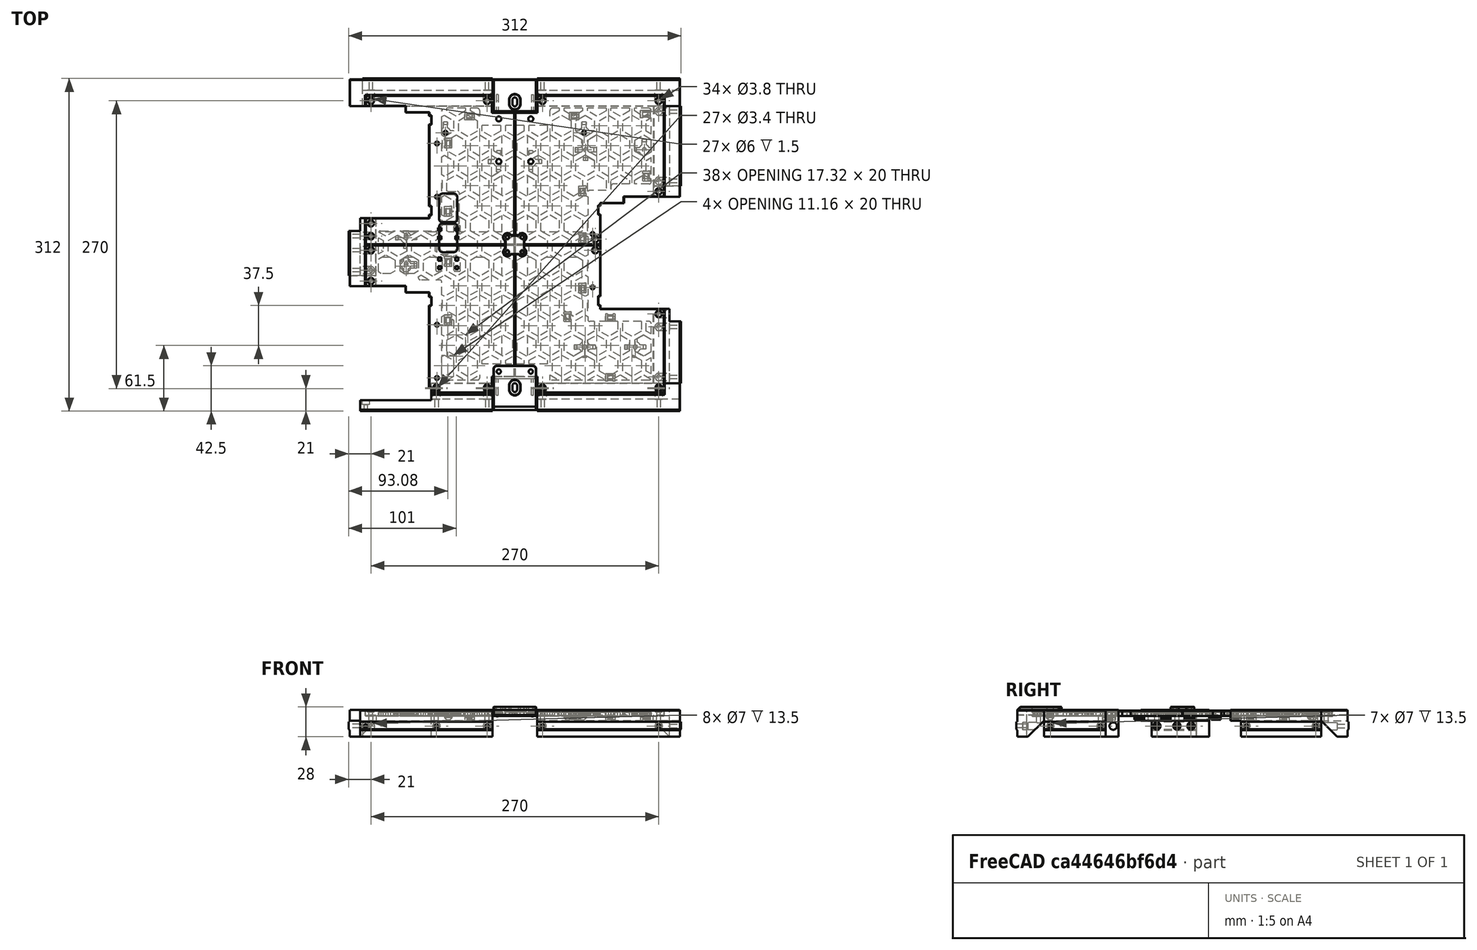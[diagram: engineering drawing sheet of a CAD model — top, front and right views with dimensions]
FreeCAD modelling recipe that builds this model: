
FCSTD DOCUMENT  (FreeCAD 0.19R24291 (Git))
Label: bottom-panel-4pcs
License: Other
LicenseURL: GPL3
objects: Part::Feature×85, Part::MultiFuse×51, Part::Cut×34, Part::Box×30, Part::Cylinder×17, Part::Chamfer×15, Part::Refine×5, Part::Fillet×4, Part::MultiCommon×4, Part::Extrusion×1
note: 246 computed .brp shape members not serialized (recipe doc carries the construction recipe); baked Part::Feature solids carry a one-line shape summary decoded from their .brp

FEATURE [Part::Feature] Chamfer005007002031002  label="origin-uni-body"
  shape: bbox 280 x 279 x 8.5 mm, 1486 faces (baked)
FEATURE [Part::Feature] Cut002015026004001  label="plain-plate"
  shape: bbox 280 x 279 x 5 mm, 52 faces (baked)
FEATURE [Part::Feature] Fusion001010002032002  label="Fusion001010002034"
  Placement = pos=(-26,135,0) rot=(0,0,1;0rad)
  shape: bbox 6 x 6 x 35 mm, 7 faces (baked)
FEATURE [Part::Feature] Fusion001010002032003  label="Fusion001010002035"
  Placement = pos=(26,135,0) rot=(0,0,1;0rad)
  shape: bbox 6 x 6 x 35 mm, 7 faces (baked)
FEATURE [Part::Feature] Fusion001010002032004  label="Fusion001010002036"
  Placement = pos=(135,135,0) rot=(0,0,1;0rad)
  shape: bbox 6 x 6 x 35 mm, 7 faces (baked)
FEATURE [Part::Feature] Fusion001010002032005  label="Fusion001010002037"
  Placement = pos=(135,50,0) rot=(0,0,1;0rad)
  shape: bbox 6 x 6 x 35 mm, 7 faces (baked)
FEATURE [Part::Feature] Fusion001010002032006  label="Fusion001010002038"
  Placement = pos=(135,-65,0) rot=(0,0,1;0rad)
  shape: bbox 6 x 6 x 35 mm, 7 faces (baked)
FEATURE [Part::Feature] Fusion001010002032007  label="Fusion001010002039"
  Placement = pos=(135,-135,0) rot=(0,0,1;0rad)
  shape: bbox 6 x 6 x 35 mm, 7 faces (baked)
FEATURE [Part::Feature] Fusion001010002032008  label="Fusion001010002040"
  Placement = pos=(-26,-135,0) rot=(0,0,1;0rad)
  shape: bbox 6 x 6 x 35 mm, 7 faces (baked)
FEATURE [Part::Feature] Fusion001010002032009  label="Fusion001010002041"
  Placement = pos=(-73.5,-135,0) rot=(0,0,1;0rad)
  shape: bbox 6 x 6 x 35 mm, 7 faces (baked)
FEATURE [Part::Feature] Fusion001010002032010  label="Fusion001010002042"
  Placement = pos=(-135,-34,0) rot=(0,0,1;0rad)
  shape: bbox 6 x 6 x 35 mm, 7 faces (baked)
FEATURE [Part::Feature] Fusion001010002032011  label="Fusion001010002043"
  Placement = pos=(-135,8,0) rot=(0,0,1;0rad)
  shape: bbox 6 x 6 x 35 mm, 7 faces (baked)
FEATURE [Part::Feature] Fusion001010002032012  label="Fusion001010002044"
  Placement = pos=(-135,135,0) rot=(0,0,1;0rad)
  shape: bbox 6 x 6 x 35 mm, 7 faces (baked)
FEATURE [Part::Feature] Fusion001010002032014
  Placement = pos=(26,-135,0) rot=(0,0,1;0rad)
  shape: bbox 6 x 6 x 35 mm, 7 faces (baked)
FEATURE [Part::Box] Box040  label="Cube039"
  AttacherType = Attacher::AttachEngine3D
  Height = 9
  Length = 15
  Placement = pos=(-70,-45,24.5) rot=(0,0,1;0rad)
  Width = 25
FEATURE [Part::Fillet] Fillet001025
  Base = -> Box040
  Edges = 4 edges r=2: [Edge1,Edge3,Edge5,Edge7]
  Placement = pos=(0,39,0) rot=(0,0,1;0rad)
FEATURE [Part::Box] Box046  label="Cube045"
  AttacherType = Attacher::AttachEngine3D
  Height = 10
  Length = 2
  Placement = pos=(-55,-6,24.5) rot=(0,0,1;0rad)
  Width = 3
FEATURE [Part::Box] Box047  label="Cube046"
  AttacherType = Attacher::AttachEngine3D
  Height = 10
  Length = 2
  Placement = pos=(-72,-14,24.5) rot=(0,0,1;0rad)
  Width = 3
FEATURE [Part::Box] Box048  label="Cube047"
  AttacherType = Attacher::AttachEngine3D
  Height = 10
  Length = 2
  Placement = pos=(-72,-6,24.5) rot=(0,0,1;0rad)
  Width = 3
FEATURE [Part::Box] Box049  label="Cube048"
  AttacherType = Attacher::AttachEngine3D
  Height = 10
  Length = 2
  Placement = pos=(-55,-14,24.5) rot=(0,0,1;0rad)
  Width = 3
FEATURE [Part::MultiFuse] Fusion006002011004053036004001028003005014008
  Placement = pos=(0,-9,0) rot=(0,0,1;0rad)
  Shapes = -> [Box046,Box048,Box047,Box049]
FEATURE [Part::MultiFuse] Fusion006002011004053036004001028003005014018004  label="cabling"
  Placement = pos=(0,28,0) rot=(0,0,1;0rad)
  Shapes = -> [Fillet001025,Fusion006002011004053036004001028003005014008]
FEATURE [Part::Feature] Cut002015002
  Placement = pos=(-102,8.5,27.5) rot=(0,1,0;3.14159rad)
  shape: bbox 20 x 20 x 3 mm, 23 faces (baked)
FEATURE [Part::Feature] Cut002015003
  Placement = pos=(-102,-18,27.5) rot=(0,1,0;3.14159rad)
  shape: bbox 20 x 20 x 3 mm, 23 faces (baked)
FEATURE [Part::Feature] Cut002015004
  Placement = pos=(113,-96,27.5) rot=(0,1,0;3.14159rad)
  shape: bbox 20 x 20 x 3 mm, 23 faces (baked)
FEATURE [Part::Feature] Cut002015005
  Placement = pos=(65.5,-96,27.5) rot=(0,1,0;3.14159rad)
  shape: bbox 20 x 20 x 3 mm, 23 faces (baked)
FEATURE [Part::Feature] Cut002015006
  Placement = pos=(121.5,89,27.5) rot=(0,1,0;3.14159rad)
  shape: bbox 20 x 20 x 3 mm, 23 faces (baked)
FEATURE [Part::Feature] Cut002015007
  Placement = pos=(66.5,89,27.5) rot=(0,1,0;3.14159rad)
  shape: bbox 20 x 20 x 3 mm, 23 faces (baked)
FEATURE [Part::Cylinder] Cylinder003
  Angle = 360
  AttacherType = Attacher::AttachEngine3D
  Height = 3.5
  Placement = pos=(66.5,89,24.5) rot=(0,0,1;0rad)
  Radius = 1.9
FEATURE [Part::Cylinder] Cylinder004
  Angle = 360
  AttacherType = Attacher::AttachEngine3D
  Height = 3.5
  Placement = pos=(121.5,89,24.5) rot=(0,0,1;0rad)
  Radius = 1.9
FEATURE [Part::Cylinder] Cylinder005
  Angle = 360
  AttacherType = Attacher::AttachEngine3D
  Height = 3.5
  Placement = pos=(113,-96,24.5) rot=(0,0,1;0rad)
  Radius = 1.9
FEATURE [Part::Cylinder] Cylinder006
  Angle = 360
  AttacherType = Attacher::AttachEngine3D
  Height = 3.5
  Placement = pos=(65.5,-96,24.5) rot=(0,0,1;0rad)
  Radius = 1.9
FEATURE [Part::Cylinder] Cylinder007
  Angle = 360
  AttacherType = Attacher::AttachEngine3D
  Height = 3.5
  Placement = pos=(-102,-18,24.5) rot=(0,0,1;0rad)
  Radius = 1.9
FEATURE [Part::Cylinder] Cylinder008
  Angle = 360
  AttacherType = Attacher::AttachEngine3D
  Height = 3.5
  Placement = pos=(-102,8.5,24.5) rot=(0,0,1;0rad)
  Radius = 1.9
FEATURE [Part::Feature] Chamfer001001  label="ziptie"
  Placement = pos=(94,-72,28) rot=(0,1,0;3.14159rad)
  shape: bbox 9 x 7 x 7 mm, 14 faces (baked)
FEATURE [Part::Feature] Chamfer005007002003  label="ziptie001"
  Placement = pos=(94,-128,28) rot=(0,1,0;3.14159rad)
  shape: bbox 9 x 7 x 7 mm, 14 faces (baked)
FEATURE [Part::Feature] Chamfer005007002005  label="ziptie003"
  Placement = pos=(-66,-20,28) rot=(0.707107,0.707107,0;3.14159rad)
  shape: bbox 7 x 9 x 7 mm, 14 faces (baked)
FEATURE [Part::Feature] Chamfer005007002006  label="ziptie004"
  Placement = pos=(-66,91,28) rot=(0.707107,0.707107,0;3.14159rad)
  shape: bbox 7 x 9 x 7 mm, 14 faces (baked)
FEATURE [Part::Feature] Chamfer005007002008  label="ziptie006"
  Placement = pos=(60,-45,28) rot=(0.707107,0.707107,0;3.14159rad)
  shape: bbox 7 x 9 x 7 mm, 14 faces (baked)
FEATURE [Part::Feature] Chamfer005007002009  label="ziptie007"
  Placement = pos=(60,2,28) rot=(0.707107,0.707107,0;3.14159rad)
  shape: bbox 7 x 9 x 7 mm, 14 faces (baked)
FEATURE [Part::Feature] Chamfer005007002010  label="ziptie008"
  Placement = pos=(60,46,28) rot=(0.707107,0.707107,0;3.14159rad)
  shape: bbox 7 x 9 x 7 mm, 14 faces (baked)
FEATURE [Part::Feature] Chamfer005007002011  label="ziptie009"
  Placement = pos=(60,117,28) rot=(0,1,0;3.14159rad)
  shape: bbox 9 x 7 x 7 mm, 14 faces (baked)
FEATURE [Part::Feature] Chamfer005007002012  label="ziptie010"
  Placement = pos=(-38,117,28) rot=(0,1,0;3.14159rad)
  shape: bbox 9 x 7 x 7 mm, 14 faces (baked)
FEATURE [Part::Feature] Chamfer005007002013  label="ziptie011"
  Placement = pos=(46,-72,28) rot=(0.707107,0.707107,0;3.14159rad)
  shape: bbox 7 x 9 x 7 mm, 14 faces (baked)
FEATURE [Part::Feature] Chamfer005007002014  label="ziptie012"
  Placement = pos=(-66,-75,28) rot=(0.707107,0.707107,0;3.14159rad)
  shape: bbox 7 x 9 x 7 mm, 14 faces (baked)
FEATURE [Part::Feature] Chamfer005007002015  label="ziptie013"
  Placement = pos=(127,119,28) rot=(0,1,0;3.14159rad)
  shape: bbox 9 x 7 x 7 mm, 14 faces (baked)
FEATURE [Part::Feature] Chamfer005007002017  label="ziptie015"
  Placement = pos=(120,60,28) rot=(0.707107,0.707107,0;3.14159rad)
  shape: bbox 7 x 9 x 7 mm, 14 faces (baked)
FEATURE [Part::Box] Box039  label="Cube038"
  AttacherType = Attacher::AttachEngine3D
  Height = 5
  Length = 21
  Placement = pos=(-73,-48,24.5) rot=(0,0,1;0rad)
  Width = 31
FEATURE [Part::Box] Box041  label="Cube040"
  AttacherType = Attacher::AttachEngine3D
  Height = 5
  Length = 15
  Placement = pos=(-70,-45,24.5) rot=(0,0,1;0rad)
  Width = 25
FEATURE [Part::Fillet] Fillet001026
  Base = -> Box039
  Edges = 4 edges r=2: [Edge1,Edge3,Edge5,Edge7]
FEATURE [Part::Fillet] Fillet001027
  Base = -> Box041
  Edges = 4 edges r=2: [Edge1,Edge3,Edge5,Edge7]
FEATURE [Part::Cut] Cut002015017
  Base = -> Fillet001026
  Placement = pos=(0,39,0) rot=(0,0,1;0rad)
  Tool = -> Fillet001027
FEATURE [Part::Box] Box050  label="Cube049"
  AttacherType = Attacher::AttachEngine3D
  Height = 5
  Length = 6
  Placement = pos=(-74,-16,24.5) rot=(0,0,1;0rad)
  Width = 15
FEATURE [Part::Box] Box053  label="Cube052"
  AttacherType = Attacher::AttachEngine3D
  Height = 5
  Length = 6
  Placement = pos=(-57,-16,24.5) rot=(0,0,1;0rad)
  Width = 15
FEATURE [Part::MultiFuse] Fusion006002011004053036004001028003005014009
  Shapes = -> [Box050,Box053]
FEATURE [Part::Fillet] Fillet001028
  Base = -> Fusion006002011004053036004001028003005014009
  Edges = 8 edges r=1: [Edge1,Edge3,Edge5,Edge7,Edge13,Edge15,Edge17,Edge19]
  Placement = pos=(0,-9,0) rot=(0,0,1;0rad)
FEATURE [Part::MultiFuse] Fusion006002011004053036004001028003005014018003
  Placement = pos=(0,28,0) rot=(0,0,1;0rad)
  Shapes = -> [Fillet001028,Cut002015017]
FEATURE [Part::Box] Box  label="Cube"
  AttacherType = Attacher::AttachEngine3D
  Height = 10
  Length = 150
  Placement = pos=(0.25,0.25,22) rot=(0,0,1;0rad)
  Width = 150
FEATURE [Part::Box] Box054  label="Cube053"
  AttacherType = Attacher::AttachEngine3D
  Height = 10
  Length = 150
  Placement = pos=(-150.25,0.25,22) rot=(0,0,1;0rad)
  Width = 150
FEATURE [Part::Box] Box055  label="Cube054"
  AttacherType = Attacher::AttachEngine3D
  Height = 10
  Length = 150
  Placement = pos=(-150.25,-150.25,22) rot=(0,0,1;0rad)
  Width = 150
FEATURE [Part::Box] Box056  label="Cube055"
  AttacherType = Attacher::AttachEngine3D
  Height = 10
  Length = 150
  Placement = pos=(0.25,-150.25,22) rot=(0,0,1;0rad)
  Width = 150
FEATURE [Part::Feature] Cut002015026004002  label="plain-plate001"
  shape: bbox 280 x 279 x 5 mm, 52 faces (baked)
FEATURE [Part::Feature] Cut002015026004003  label="plain-plate002"
  shape: bbox 280 x 279 x 5 mm, 52 faces (baked)
FEATURE [Part::Feature] Cut002015026004004  label="plain-plate003"
  shape: bbox 280 x 279 x 5 mm, 52 faces (baked)
FEATURE [Part::Feature] Cut002015026004005  label="plain-plate004"
  shape: bbox 280 x 279 x 5 mm, 52 faces (baked)
FEATURE [Part::MultiCommon] Common  label="fr-panel"
  Shapes = -> [Cut002015026004002,Box056]
FEATURE [Part::MultiCommon] Common001  label="fl-panel"
  Shapes = -> [Cut002015026004003,Box055]
FEATURE [Part::MultiCommon] Common002  label="bl-panel"
  Shapes = -> [Cut002015026004004,Box054]
FEATURE [Part::MultiCommon] Common003  label="br-panel"
  Shapes = -> [Cut002015026004005,Box]
FEATURE [Part::Feature] Cut002015026005001  label="hex-grid"
  shape: bbox 256 x 255 x 5 mm, 921 faces, 122 solids (baked)
FEATURE [Part::Feature] Cut002015026005002  label="hex-grid001"
  shape: bbox 256 x 255 x 5 mm, 921 faces, 122 solids (baked)
FEATURE [Part::Feature] Cut002015026005003  label="hex-grid002"
  shape: bbox 256 x 255 x 5 mm, 921 faces, 122 solids (baked)
FEATURE [Part::Feature] Cut002015026005004  label="hex-grid003"
  shape: bbox 256 x 255 x 5 mm, 921 faces, 122 solids (baked)
FEATURE [Part::Cut] Cut
  Base = -> Common001
  Tool = -> Cut002015026005002
FEATURE [Part::Cut] Cut002015026005005
  Base = -> Common
  Tool = -> Cut002015026005001
FEATURE [Part::Cut] Cut002015026005006
  Base = -> Common002
  Tool = -> Cut002015026005003
FEATURE [Part::Cut] Cut002015026005007
  Base = -> Common003
  Tool = -> Cut002015026005004
FEATURE [Part::Feature] Fusion006002011004053036004001028003005014018008
  Placement = pos=(-135,-5.25,0) rot=(0,0,1;0rad)
  shape: bbox 6 x 6 x 35 mm, 7 faces (baked)
FEATURE [Part::Feature] Fusion006002011004053036004001028003005014018009
  Placement = pos=(75.5,-5.25,0) rot=(0,0,1;0rad)
  shape: bbox 6 x 6 x 35 mm, 7 faces (baked)
FEATURE [Part::Feature] Fusion006002011004053036004001028003005014018010
  Placement = pos=(75.5,5.25,0) rot=(0,0,1;0rad)
  shape: bbox 6 x 6 x 35 mm, 7 faces (baked)
FEATURE [Part::MultiFuse] Fusion006002011004053036004001028003005014018013
  Shapes = -> [Fusion001010002032003,Fusion001010002032004,Fusion001010002032005,Fusion006002011004053036004001028003005014018010]
FEATURE [Part::Cut] Cut002015026005011
  Base = -> Cut002015026005007
  Tool = -> Fusion006002011004053036004001028003005014018013
FEATURE [Part::Cylinder] Cylinder
  Angle = 360
  AttacherType = Attacher::AttachEngine3D
  Height = 10
  Placement = pos=(7,7,21.5) rot=(0,0,1;0rad)
  Radius = 2
FEATURE [Part::Cylinder] Cylinder009
  Angle = 360
  AttacherType = Attacher::AttachEngine3D
  Height = 10
  Placement = pos=(-7,7,21.5) rot=(0,0,1;0rad)
  Radius = 2
FEATURE [Part::Cylinder] Cylinder010
  Angle = 360
  AttacherType = Attacher::AttachEngine3D
  Height = 10
  Placement = pos=(7,-7,21.5) rot=(0,0,1;0rad)
  Radius = 2
FEATURE [Part::Cylinder] Cylinder011
  Angle = 360
  AttacherType = Attacher::AttachEngine3D
  Height = 10
  Placement = pos=(-7,-7,21.5) rot=(0,0,1;0rad)
  Radius = 2
FEATURE [Part::Cylinder] Cylinder012
  Angle = 360
  AttacherType = Attacher::AttachEngine3D
  Height = 10
  Placement = pos=(15,118,22) rot=(0,0,1;0rad)
  Radius = 2
FEATURE [Part::Cylinder] Cylinder013
  Angle = 360
  AttacherType = Attacher::AttachEngine3D
  Height = 10
  Placement = pos=(15,-119,22) rot=(0,0,1;0rad)
  Radius = 2
FEATURE [Part::Cylinder] Cylinder014
  Angle = 360
  AttacherType = Attacher::AttachEngine3D
  Height = 10
  Placement = pos=(-15,118,22) rot=(0,0,1;0rad)
  Radius = 2
FEATURE [Part::Cylinder] Cylinder015
  Angle = 360
  AttacherType = Attacher::AttachEngine3D
  Height = 10
  Placement = pos=(-15,-119,22) rot=(0,0,1;0rad)
  Radius = 2
FEATURE [Part::MultiFuse] Fusion006002011004053036004001028003005014018014
  Shapes = -> [Cylinder009,Cylinder014]
FEATURE [Part::MultiFuse] Fusion006002011004053036004001028003005014018015
  Shapes = -> [Cylinder,Cylinder012]
FEATURE [Part::Cut] Cut002015026005013
  Base = -> Cut002015026005011
  Tool = -> Fusion006002011004053036004001028003005014018015
FEATURE [Part::MultiFuse] Fusion006002011004053036004001028003005014018025
  Shapes = -> [Cylinder003,Cylinder004]
FEATURE [Part::MultiFuse] Fusion006002011004053036004001028003005014018028
  Shapes = -> [Cylinder006,Cylinder005]
FEATURE [Part::Feature] Extrude001001  label="134mm0length001"
  Placement = pos=(-21,-129,0) rot=(0,0,1;3.14159rad)
  shape: bbox 134 x 26 x 25 mm, 16 faces (baked)
FEATURE [Part::Feature] Fusion001010002017  label="bolt-slot016"
  Placement = pos=(-140,-134,0) rot=(0,0,1;1.5708rad)
  shape: bbox 7 x 31 x 40 mm, 9 faces (baked)
FEATURE [Part::Feature] Cut002001  label="Cut009"
  Placement = pos=(5,0,0) rot=(0,0,1;0rad)
  shape: bbox 119 x 26 x 25 mm, 18 faces (baked)
FEATURE [Part::Box] Box062  label="Cube061"
  AttacherType = Attacher::AttachEngine3D
  Height = 33
  Length = 10
  Placement = pos=(-88.5,-145,2.5) rot=(0,0,1;0rad)
  Width = 18
FEATURE [Part::Box] Box022  label="Cube021"
  AttacherType = Attacher::AttachEngine3D
  Height = 40
  Length = 111
  Placement = pos=(124.5,-176,0) rot=(0,0,1;0rad)
  Width = 47
FEATURE [Part::Feature] Fusion001010002009  label="bolt-slot008"
  Placement = pos=(135,125,0) rot=(0,0,1;3.14159rad)
  shape: bbox 31 x 7 x 40 mm, 9 faces (baked)
FEATURE [Part::Box] Box021  label="Cube020"
  AttacherType = Attacher::AttachEngine3D
  Height = 40
  Length = 111
  Placement = pos=(117.5,130,0) rot=(0,0,1;0rad)
  Width = 47
FEATURE [Part::Box] Box038  label="Cube037"
  AttacherType = Attacher::AttachEngine3D
  Height = 20
  Length = 42
  Placement = pos=(124,13,0) rot=(0,0,1;0rad)
  Width = 42
FEATURE [Part::Feature] Fusion006002011004053036004001028003005014005  label="bolt-slot020"
  Placement = pos=(135,60,0) rot=(0,0,1;3.14159rad)
  shape: bbox 31 x 7 x 40 mm, 9 faces (baked)
FEATURE [Part::Feature] Fusion001010002015  label="bolt-slot014"
  Placement = pos=(-26,-134,0) rot=(0,0,1;1.5708rad)
  shape: bbox 7 x 31 x 40 mm, 9 faces (baked)
FEATURE [Part::Feature] Fusion001010002003  label="bolt-slot003"
  Placement = pos=(-135,-34,0) rot=(0,0,1;0rad)
  shape: bbox 31 x 7 x 40 mm, 9 faces (baked)
FEATURE [Part::Box] Box020  label="Cube019"
  AttacherType = Attacher::AttachEngine3D
  Height = 40
  Length = 111
  Placement = pos=(117.5,-2,0) rot=(0,0,1;0rad)
  Width = 47
FEATURE [Part::Box] Box019  label="Cube018"
  AttacherType = Attacher::AttachEngine3D
  Height = 40
  Length = 111
  Placement = pos=(-256,13,0) rot=(0,0,1;0rad)
  Width = 59
FEATURE [Part::Box] Box015  label="Cube014"
  AttacherType = Attacher::AttachEngine3D
  Height = 40
  Length = 111
  Placement = pos=(-191.5,-145,0) rot=(0,0,1;0rad)
  Width = 47
FEATURE [Part::Feature] Fusion001010002002  label="bolt-slot002"
  Placement = pos=(-135,8,0) rot=(0,0,1;0rad)
  shape: bbox 31 x 7 x 40 mm, 9 faces (baked)
FEATURE [Part::Box] Box017  label="Cube016"
  AttacherType = Attacher::AttachEngine3D
  Height = 40
  Length = 111
  Placement = pos=(-193,-86,0) rot=(0,0,1;0rad)
  Width = 47
FEATURE [Part::Feature] Fusion001010002010  label="bolt-slot009"
  Placement = pos=(135,50,0) rot=(0,0,1;3.14159rad)
  shape: bbox 31 x 7 x 40 mm, 9 faces (baked)
FEATURE [Part::Box] Box024  label="Cube023"
  AttacherType = Attacher::AttachEngine3D
  Height = 40
  Length = 111
  Placement = pos=(145,-72,0) rot=(0,0,1;0rad)
  Width = 47
FEATURE [Part::MultiFuse] Fusion006002011004053036004001028003005014006
  Shapes = -> [Fusion006002011004053036004001028003005014005,Fusion001010002009,Fusion001010002010]
FEATURE [Part::Feature] Fusion006002011004053036004001028003005014003  label="bolt-slot019"
  Placement = pos=(-135,-24,0) rot=(0,0,1;0rad)
  shape: bbox 31 x 7 x 40 mm, 9 faces (baked)
FEATURE [Part::Feature] Extrude001005  label="134mm0length005"
  Placement = pos=(-130,-61,0) rot=(0,0,1;1.5708rad)
  shape: bbox 26 x 134 x 25 mm, 16 faces (baked)
FEATURE [Part::Feature] Extrude001006  label="134mm0length006"
  Placement = pos=(130,-19,0) rot=(0,0,-1;1.5708rad)
  shape: bbox 26 x 134 x 25 mm, 16 faces (baked)
FEATURE [Part::Feature] Fusion001010002016  label="bolt-slot015"
  Placement = pos=(-73.5,-134,0) rot=(0,0,1;1.5708rad)
  shape: bbox 7 x 31 x 40 mm, 9 faces (baked)
FEATURE [Part::MultiFuse] Fusion006002011004053036004001028003005014018029
  Shapes = -> [Fusion001010002017,Fusion001010002016,Fusion001010002015]
FEATURE [Part::Feature] Fusion001010002013  label="bolt-slot012"
  Placement = pos=(135,-134,0) rot=(0,0,1;1.5708rad)
  shape: bbox 7 x 31 x 40 mm, 9 faces (baked)
FEATURE [Part::Feature] Fusion001010002012  label="bolt-slot011"
  Placement = pos=(135,-124,0) rot=(0,0,1;3.14159rad)
  shape: bbox 31 x 7 x 40 mm, 9 faces (baked)
FEATURE [Part::Feature] Extrude001007  label="134mm0length007"
  Placement = pos=(130,167,0) rot=(0,0,-1;1.5708rad)
  shape: bbox 26 x 134 x 25 mm, 16 faces (baked)
FEATURE [Part::Feature] Fusion001010002008  label="bolt-slot007"
  Placement = pos=(135,135,0) rot=(0,0,-1;1.5708rad)
  shape: bbox 7 x 31 x 40 mm, 9 faces (baked)
FEATURE [Part::Box] Box018  label="Cube017"
  AttacherType = Attacher::AttachEngine3D
  Height = 40
  Length = 111
  Placement = pos=(-193,25,0) rot=(0,0,1;0rad)
  Width = 59
FEATURE [Part::Box] Box016  label="Cube015"
  AttacherType = Attacher::AttachEngine3D
  Height = 40
  Length = 111
  Placement = pos=(-256,-178.5,0) rot=(0,0,1;0rad)
  Width = 47
FEATURE [Part::MultiFuse] Fusion001004
  Shapes = -> [Box016,Box015]
FEATURE [Part::MultiFuse] Fusion001005
  Shapes = -> [Box019,Box018,Box017]
FEATURE [Part::Cut] Cut003
  Base = -> Extrude001005
  Tool = -> Fusion001005
FEATURE [Part::MultiFuse] Fusion001006
  Shapes = -> [Box021,Box020]
FEATURE [Part::Cut] Cut004
  Base = -> Extrude001007
  Tool = -> Fusion001006
FEATURE [Part::Cut] Cut002015014
  Base = -> Cut004
  Tool = -> Fusion006002011004053036004001028003005014006
FEATURE [Part::Cut] Cut002015015  label="panel-mount-BMR"
  Base = -> Cut002015014
  Tool = -> Box038
FEATURE [Part::Chamfer] Chamfer005007002023
  Base = -> Cut002015015
  Edges = 1 edges r=0.99: [Edge40]
FEATURE [Part::Feature] Fusion001010001  label="Fusion001011"
  shape: bbox 134 x 26 x 25 mm, 15 faces (baked)
FEATURE [Part::Chamfer] Chamfer002
  Base = -> Fusion001010001
  Edges = 4 edges r=0.4: [Edge9,Edge32,Edge35,Edge37]
FEATURE [Part::Box] Box036  label="Cube035"
  AttacherType = Attacher::AttachEngine3D
  Height = 20
  Length = 12
  Placement = pos=(-155,116,0) rot=(0,0,1;0rad)
  Width = 42
FEATURE [Part::Feature] Fusion001010002005  label="bolt-slot004"
  Placement = pos=(-26,135,0) rot=(0,0,-1;1.5708rad)
  shape: bbox 7 x 31 x 40 mm, 9 faces (baked)
FEATURE [Part::Cut] Cut002
  Base = -> Extrude001001
  Tool = -> Fusion001004
FEATURE [Part::MultiFuse] Fusion001010002022
  Shapes = -> [Cut002001,Cut002]
FEATURE [Part::Cut] Cut002015026002
  Base = -> Fusion001010002022
  Tool = -> Fusion006002011004053036004001028003005014018029
FEATURE [Part::Cut] Cut002015026003
  Base = -> Cut002015026002
  Tool = -> Box062
FEATURE [Part::Chamfer] Chamfer005007002029
  Base = -> Cut002015026003
  Edges = 1 edges r=0.99: [Edge82]
  Placement = pos=(0,-1,0) rot=(0,0,1;0rad)
FEATURE [Part::Feature] Fusion001010002023  label="bolt-slot017"
  Placement = pos=(135,-77,0) rot=(0,0,1;3.14159rad)
  shape: bbox 31 x 7 x 40 mm, 9 faces (baked)
FEATURE [Part::Feature] Fusion001008001  label="Fusion001013"
  shape: bbox 134 x 26 x 25 mm, 15 faces (baked)
FEATURE [Part::Chamfer] Chamfer004
  Base = -> Fusion001008001
  Edges = 4 edges r=0.4: [Edge2,Edge16,Edge19,Edge38]
FEATURE [Part::Feature] Fusion001010002006  label="bolt-slot005"
  Placement = pos=(-135,135,0) rot=(0,0,-1;1.5708rad)
  shape: bbox 7 x 31 x 40 mm, 9 faces (baked)
FEATURE [Part::MultiFuse] Fusion001010002026
  Shapes = -> [Fusion001010002006,Fusion001010002005]
FEATURE [Part::Cut] Cut002003
  Base = -> Chamfer002
  Tool = -> Fusion001010002026
FEATURE [Part::Box] Box037  label="Cube036"
  AttacherType = Attacher::AttachEngine3D
  Height = 20
  Length = 42
  Placement = pos=(-166,-71,0) rot=(0,0,1;0rad)
  Width = 42
FEATURE [Part::Cut] Cut002015010  label="panel-mount-BL"
  Base = -> Cut002003
  Tool = -> Box036
FEATURE [Part::Chamfer] Chamfer005007002025
  Base = -> Cut002015010
  Edges = 1 edges r=0.99: [Edge41]
FEATURE [Part::Feature] Fusion001010002014  label="bolt-slot013"
  Placement = pos=(26,-134,0) rot=(0,0,1;1.5708rad)
  shape: bbox 7 x 31 x 40 mm, 9 faces (baked)
FEATURE [Part::MultiFuse] Fusion006002011004053036004001028003005014002
  Shapes = -> [Fusion001010002013,Fusion001010002014]
FEATURE [Part::Cut] Cut002015011  label="panel-mount-FR"
  Base = -> Chamfer004
  Tool = -> Fusion006002011004053036004001028003005014002
FEATURE [Part::Chamfer] Chamfer005007002021
  Base = -> Cut002015011
  Edges = 1 edges r=0.99: [Edge36]
  Placement = pos=(0,-1,0) rot=(0,0,1;0rad)
FEATURE [Part::Feature] Fusion001010002011  label="bolt-slot010"
  Placement = pos=(135,-65,0) rot=(0,0,1;3.14159rad)
  shape: bbox 31 x 7 x 40 mm, 9 faces (baked)
FEATURE [Part::Feature] Fusion001009001  label="Fusion001012"
  shape: bbox 134 x 26 x 25 mm, 15 faces (baked)
FEATURE [Part::Chamfer] Chamfer003
  Base = -> Fusion001009001
  Edges = 4 edges r=0.4: [Edge19,Edge21,Edge24,Edge39]
FEATURE [Part::Feature] Fusion001010002007  label="bolt-slot006"
  Placement = pos=(26,135,0) rot=(0,0,-1;1.5708rad)
  shape: bbox 7 x 31 x 40 mm, 9 faces (baked)
FEATURE [Part::MultiFuse] Fusion001010002027
  Shapes = -> [Fusion001010002008,Fusion001010002007]
FEATURE [Part::Cut] Cut002004  label="panel-mount-BR"
  Base = -> Chamfer003
  Tool = -> Fusion001010002027
FEATURE [Part::Chamfer] Chamfer005007002024
  Base = -> Cut002004
  Edges = 1 edges r=0.99: [Edge27]
FEATURE [Part::MultiFuse] Fusion001010002029
  Shapes = -> [Fusion001010002012,Fusion001010002023,Fusion001010002011]
FEATURE [Part::Box] Box023  label="Cube022"
  AttacherType = Attacher::AttachEngine3D
  Height = 40
  Length = 111
  Placement = pos=(124.5,-60,0) rot=(0,0,1;0rad)
  Width = 47
FEATURE [Part::MultiFuse] Fusion001007
  Shapes = -> [Box022,Box024,Box023]
FEATURE [Part::Cut] Cut005
  Base = -> Extrude001006
  Tool = -> Fusion001007
FEATURE [Part::Cut] Cut002006  label="panel-mount-FMR"
  Base = -> Cut005
  Tool = -> Fusion001010002029
FEATURE [Part::Chamfer] Chamfer005007002022
  Base = -> Cut002006
  Edges = 1 edges r=0.99: [Edge56]
FEATURE [Part::Feature] Fusion006002011004053036004001028003005014018030  label="bolt-slot021"
  Placement = pos=(-135,-5.25,0) rot=(0,0,1;0rad)
  shape: bbox 31 x 7 x 40 mm, 9 faces (baked)
FEATURE [Part::MultiFuse] Fusion006002011004053036004001028003005014018031
  Shapes = -> [Fusion001010002002,Fusion006002011004053036004001028003005014018030,Fusion006002011004053036004001028003005014003,Fusion001010002003]
FEATURE [Part::Cut] Cut002015026005020002
  Base = -> Cut003
  Tool = -> Fusion006002011004053036004001028003005014018031
FEATURE [Part::Cut] Cut002015026005020003
  Base = -> Cut002015026005020002
  Tool = -> Box037
FEATURE [Part::Chamfer] Chamfer005007002031007
  Base = -> Cut002015026005020003
  Edges = 1 edges r=0.99: [Edge78]
FEATURE [Part::MultiFuse] Fusion006002011004053036004001028003005014018032
  Shapes = -> [Fusion001010002032002,Fusion001010002032012,Fusion001010002032011]
FEATURE [Part::Cut] Cut002015026005020004
  Base = -> Cut002015026005006
  Tool = -> Fusion006002011004053036004001028003005014018032
FEATURE [Part::Cut] Cut002015026005020005
  Base = -> Cut002015026005020004
  Tool = -> Fusion006002011004053036004001028003005014018014
FEATURE [Part::Feature] Chamfer003001
  Placement = pos=(-8e-15,140,25) rot=(0,0,1;3.14159rad)
  shape: bbox 40 x 30 x 6 mm, 49 faces (baked)
FEATURE [Part::Cylinder] Cylinder016
  Angle = 360
  AttacherType = Attacher::AttachEngine3D
  Height = 10
  Placement = pos=(-15,78,23) rot=(0,0,1;0rad)
  Radius = 2
FEATURE [Part::Cylinder] Cylinder017
  Angle = 360
  AttacherType = Attacher::AttachEngine3D
  Height = 10
  Placement = pos=(15,78,23) rot=(0,0,1;0rad)
  Radius = 2
FEATURE [Part::Feature] Cut002015026005020007004
  Placement = pos=(0,0,30) rot=(0,0,1;0rad)
  shape: bbox 22 x 22 x 3 mm, 24 faces (baked)
FEATURE [Part::Feature] Cut001001
  Placement = pos=(0,-140,25) rot=(0,0,1;0rad)
  shape: bbox 40 x 41.5 x 9 mm, 50 faces (baked)
FEATURE [Part::Feature] Chamfer005007002022_cs
  shape: bbox 26 x 4e-07 x 25 mm, 0 faces, 0 solids (baked)
FEATURE [Part::Extrusion] Extrude
  Base = -> Chamfer005007002022_cs
  Dir = (0,1,0)
  DirMode = 2
  FaceMakerClass = Part::FaceMakerBullseye
  LengthFwd = 1
  LengthRev = 0
  Placement = pos=(0,-36,0) rot=(0,0,1;0rad)
  Solid = true
  Symmetric = false
FEATURE [Part::MultiFuse] Fusion006002011004053036004001028003005014018035
  Shapes = -> [Chamfer005007002022,Extrude]
FEATURE [Part::MultiFuse] Fusion
  Shapes = -> [Fusion001010002032008,Fusion001010002032009,Fusion001010002032010,Fusion006002011004053036004001028003005014018008]
FEATURE [Part::Cut] Cut002015026005020007005
  Base = -> Cut
  Tool = -> Fusion
FEATURE [Part::MultiFuse] Fusion006002011004053036004001028003005014018036
  Shapes = -> [Cylinder015,Cylinder011]
FEATURE [Part::Cut] Cut002015026005020007006
  Base = -> Cut002015026005020007005
  Tool = -> Fusion006002011004053036004001028003005014018036
FEATURE [Part::MultiFuse] Fusion006002011004053036004001028003005014018038
  Shapes = -> [Fusion001010002032014,Fusion001010002032007,Fusion001010002032006,Fusion006002011004053036004001028003005014018009]
FEATURE [Part::MultiFuse] Fusion006002011004053036004001028003005014018039
  Shapes = -> [Cylinder010,Cylinder013]
FEATURE [Part::Cut] Cut002015026005020007008
  Base = -> Cut002015026005005
  Tool = -> Fusion006002011004053036004001028003005014018039
FEATURE [Part::Cut] Cut002015026005020007009
  Base = -> Cut002015026005020007008
  Tool = -> Fusion006002011004053036004001028003005014018038
FEATURE [Part::Box] Box063  label="Cube062"
  AttacherType = Attacher::AttachEngine3D
  Height = 5
  Length = 57.5
  Placement = pos=(-78.5,-140,24.5) rot=(0,0,1;0rad)
  Width = 1
FEATURE [Part::Box] Box064  label="Cube063"
  AttacherType = Attacher::AttachEngine3D
  Height = 5
  Length = 119
  Placement = pos=(21,-140,24.5) rot=(0,0,1;0rad)
  Width = 1
FEATURE [Part::Refine] Fusion006002011004053036004001028003005014018035002
  Source = -> Fusion006002011004053036004001028003005014018035
FEATURE [Part::Feature] Cut002015026005020007011
  Placement = pos=(-15,78,27.5) rot=(0,1,0;3.14159rad)
  shape: bbox 20 x 20 x 3 mm, 23 faces (baked)
FEATURE [Part::Box] Box065  label="Cube064"
  AttacherType = Attacher::AttachEngine3D
  Height = 10
  Length = 10
  Placement = pos=(-107,-9,20) rot=(0,0,1;0rad)
  Width = 10
FEATURE [Part::Cut] Cut002015026005020007012
  Base = -> Cut002015002
  Tool = -> Box065
FEATURE [Part::MultiFuse] Fusion006002011004053036004001028003005014018035004004
  Shapes = -> [Cylinder008,Cylinder016]
FEATURE [Part::Feature] Cut002015026005020007014002
  Placement = pos=(15,78,27.5) rot=(0,1,0;3.14159rad)
  shape: bbox 20 x 20 x 3 mm, 23 faces (baked)
FEATURE [Part::MultiFuse] Fusion006002011004053036004001028003005014018035004005
  Shapes = -> [Cut002015006,Cut002015007,Cut002015026005020007014002]
FEATURE [Part::Feature] Fusion006002011004053036004001028003005014018035004005001
  Placement = pos=(0,0,0.5) rot=(0,0,1;0rad)
  shape: bbox 126.5 x 31 x 3 mm, 69 faces, 3 solids (baked)
FEATURE [Part::MultiFuse] Fusion006002011004053036004001028003005014018035004005002
  Shapes = -> [Fusion006002011004053036004001028003005014018035004005001,Fusion006002011004053036004001028003005014018035004005]
FEATURE [Part::MultiFuse] Fusion006002011004053036004001028003005014018035004005003
  Shapes = -> [Chamfer005007002009,Chamfer005007002010,Chamfer005007002017,Chamfer005007002015,Chamfer005007002011]
FEATURE [Part::MultiFuse] Fusion006002011004053036004001028003005014018035004005004
  Shapes = -> [Fusion006002011004053036004001028003005014018035004005003,Fusion006002011004053036004001028003005014018035004005002]
FEATURE [Part::MultiFuse] Fusion006002011004053036004001028003005014018035004005005
  Shapes = -> [Cut002015026005013,Fusion006002011004053036004001028003005014018035004005004]
FEATURE [Part::MultiFuse] Fusion006002011004053036004001028003005014018035004005006
  Shapes = -> [Fusion006002011004053036004001028003005014018025,Cylinder017]
FEATURE [Part::Cut] Cut002015026005020007014003
  Base = -> Fusion006002011004053036004001028003005014018035004005005
  Tool = -> Fusion006002011004053036004001028003005014018035004005006
FEATURE [Part::MultiFuse] Fusion006002011004053036004001028003005014018035004005007
  Shapes = -> [Cut002015005,Cut002015004]
FEATURE [Part::Feature] Fusion006002011004053036004001028003005014018035004005007001
  Placement = pos=(0,0,0.5) rot=(0,0,1;0rad)
  shape: bbox 67.5 x 20 x 3 mm, 46 faces, 2 solids (baked)
FEATURE [Part::MultiFuse] Fusion006002011004053036004001028003005014018035004005007002
  Shapes = -> [Fusion006002011004053036004001028003005014018035004005007001,Fusion006002011004053036004001028003005014018035004005007]
FEATURE [Part::MultiFuse] Fusion006002011004053036004001028003005014018035004005007003
  Shapes = -> [Chamfer001001,Chamfer005007002003,Chamfer005007002008,Chamfer005007002013]
FEATURE [Part::MultiFuse] Fusion006002011004053036004001028003005014018035004005007004
  Shapes = -> [Fusion006002011004053036004001028003005014018035004005007002,Fusion006002011004053036004001028003005014018035004005007003]
FEATURE [Part::MultiFuse] Fusion006002011004053036004001028003005014018035004005007005
  Shapes = -> [Cut002015026005020007009,Fusion006002011004053036004001028003005014018035004005007004]
FEATURE [Part::Cut] Cut002015026005020007014004
  Base = -> Fusion006002011004053036004001028003005014018035004005007005
  Tool = -> Fusion006002011004053036004001028003005014018028
FEATURE [Part::Feature] Cut002015026005020007014005
  Placement = pos=(-102,-18,28) rot=(0,1,0;3.14159rad)
  shape: bbox 20 x 20 x 3 mm, 23 faces (baked)
FEATURE [Part::MultiFuse] Fusion006002011004053036004001028003005014018035004005007006
  Shapes = -> [Cut002015026005020007014005,Cut002015003]
FEATURE [Part::MultiFuse] Fusion006002011004053036004001028003005014018035004005007007
  Shapes = -> [Chamfer005007002014,Chamfer005007002005]
FEATURE [Part::MultiFuse] Fusion006002011004053036004001028003005014018035004005007008
  Shapes = -> [Fusion006002011004053036004001028003005014018035004005007007,Fusion006002011004053036004001028003005014018035004005007006]
FEATURE [Part::MultiFuse] Fusion006002011004053036004001028003005014018035004005007009
  Shapes = -> [Cut002015026005020007006,Fusion006002011004053036004001028003005014018035004005007008]
FEATURE [Part::MultiFuse] Fusion006002011004053036004001028003005014018035004005007010
  Shapes = -> [Cut002015026005020007014004,Box064]
FEATURE [Part::Cut] Cut002015026005020007014006
  Base = -> Fusion006002011004053036004001028003005014018035004005007009
  Tool = -> Cylinder007
FEATURE [Part::MultiFuse] Fusion006002011004053036004001028003005014018035004005007011
  Shapes = -> [Cut002015026005020007014006,Box063]
FEATURE [Part::MultiFuse] Fusion006002011004053036004001028003005014018035004005007012
  Shapes = -> [Cut002015026005020007011,Cut002015026005020007012]
FEATURE [Part::Feature] Fusion006002011004053036004001028003005014018035004005007012001
  Placement = pos=(0,0,0.5) rot=(0,0,1;0rad)
  shape: bbox 107 x 87 x 3 mm, 45 faces, 2 solids (baked)
FEATURE [Part::MultiFuse] Fusion006002011004053036004001028003005014018035004005007012002
  Shapes = -> [Fusion006002011004053036004001028003005014018035004005007012,Fusion006002011004053036004001028003005014018035004005007012001]
FEATURE [Part::MultiFuse] Fusion006002011004053036004001028003005014018035004005007012003
  Shapes = -> [Chamfer005007002006,Chamfer005007002012]
FEATURE [Part::MultiFuse] Fusion006002011004053036004001028003005014018035004005007012004
  Shapes = -> [Fusion006002011004053036004001028003005014018003,Fusion006002011004053036004001028003005014018035004005007012002,Fusion006002011004053036004001028003005014018035004005007012003]
FEATURE [Part::MultiFuse] Fusion006002011004053036004001028003005014018035004005007012005
  Shapes = -> [Cut002015026005020005,Fusion006002011004053036004001028003005014018035004005007012004]
FEATURE [Part::MultiFuse] Fusion006002011004053036004001028003005014018035004005007012006
  Shapes = -> [Fusion006002011004053036004001028003005014018004,Fusion006002011004053036004001028003005014018035004004]
FEATURE [Part::Cut] Cut002015026005020007014007
  Base = -> Fusion006002011004053036004001028003005014018035004005007012005
  Tool = -> Fusion006002011004053036004001028003005014018035004005007012006
FEATURE [Part::Refine] Cut002015026005020007014007001
  Source = -> Cut002015026005020007014007
FEATURE [Part::Refine] Fusion006002011004053036004001028003005014018035004005007011001
  Source = -> Fusion006002011004053036004001028003005014018035004005007011
FEATURE [Part::Refine] Fusion006002011004053036004001028003005014018035004005007010001
  Source = -> Fusion006002011004053036004001028003005014018035004005007010
FEATURE [Part::Refine] Cut002015026005020007014003001
  Source = -> Cut002015026005020007014003
FEATURE [Part::Chamfer] Chamfer
  Base = -> Cut002015026005020007014007001
  Edges = 22 edges r=1: [Edge81,Edge82,Edge83,Edge84,Edge85,Edge86,Edge87,Edge88,Edge245,Edge252,Edge258,Edge345,Edge347,Edge697,Edge717,Edge721,Edge729,Edge752,Edge753,Edge754,Edge755,Edge757]
FEATURE [Part::Chamfer] Chamfer005007002031008
  Base = -> Chamfer
  Edges = 23 edges r=0.4: [Edge252,Edge254,Edge256,Edge259,Edge260,Edge262,Edge264,Edge267,Edge268,Edge270,Edge272,Edge275,Edge277,Edge279,Edge281,Edge283,Edge285,Edge287,Edge289,Edge290,Edge671,Edge673,Edge675]
FEATURE [Part::Chamfer] Chamfer005007002031009
  Base = -> Cut002015026005020007014003001
  Edges = 17 edges r=0.4: [Edge3,Edge6,Edge8,Edge11,Edge15,Edge17,Edge20,Edge24,Edge28,Edge30,Edge34,Edge37,Edge40,Edge42,Edge43,Edge46,Edge47]
FEATURE [Part::Chamfer] Chamfer005007002031010
  Base = -> Fusion006002011004053036004001028003005014018035004005007011001
  Edges = 18 edges r=0.4: [Edge3,Edge5,Edge8,Edge12,Edge15,Edge17,Edge20,Edge24,Edge29,Edge30,Edge35,Edge38,Edge41,Edge44,Edge46,Edge47,Edge52,Edge53]
FEATURE [Part::Chamfer] Chamfer005007002031011
  Base = -> Fusion006002011004053036004001028003005014018035004005007010001
  Edges = 14 edges r=0.4: [Edge3,Edge5,Edge11,Edge13,Edge15,Edge18,Edge22,Edge25,Edge27,Edge32,Edge34,Edge35,Edge40,Edge41]
FEATURE [Part::Feature] Chamfer005007002031011001
  shape: bbox 139.8 x 139.8 x 8.5 mm, 353 faces (baked)
FEATURE [Part::Feature] Chamfer005007002031010001
  shape: bbox 139.8 x 139.8 x 8.5 mm, 275 faces (baked)
FEATURE [Part::Feature] Chamfer005007002031009001
  shape: bbox 139.8 x 139.8 x 8.5 mm, 425 faces (baked)
FEATURE [Part::Feature] Chamfer005007002031008001
  shape: bbox 139.8 x 139.8 x 8.5 mm, 330 faces (baked)
FEATURE [Part::Cylinder] Cylinder018
  Angle = 360
  AttacherType = Attacher::AttachEngine3D
  Height = 10
  Placement = pos=(-140,-140,15) rot=(1,0,0;1.5708rad)
  Radius = 3.5
FEATURE [Part::Cut] Cut002015026005020007014007002
  Base = -> Chamfer005007002029
  Tool = -> Cylinder018
